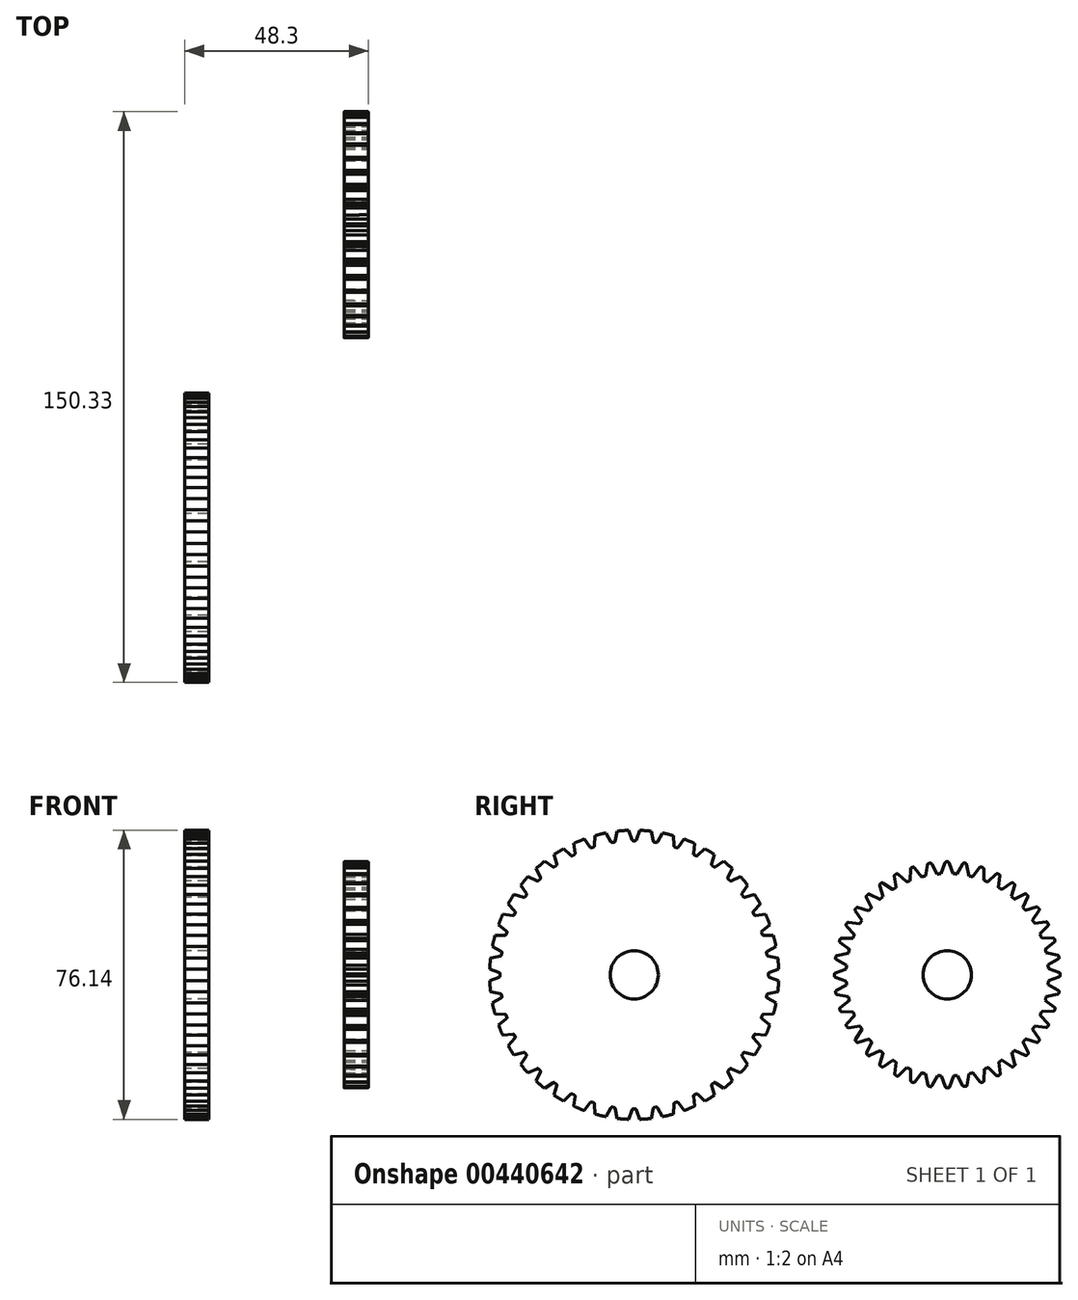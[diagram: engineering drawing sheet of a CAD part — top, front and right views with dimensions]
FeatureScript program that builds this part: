
annotation { "Feature Type Name" : "Feature", "Feature Type Description" : "" }
export const myFeature = defineFeature(function(context is Context, id is Id, definition is map)
    precondition{}
    {
        {
            var Q0;
            Q0=qCreatedBy(makeId("Front.planeOp"),FACE);
            var sketch = newSketch(context, id + "F0", { "sketchPlane" : qUnion([Q0])});
            skLineSegment(sketch, "E0", {"start": v(-6.35, 0) * mm, "end": v(0, 0) * mm, "construction": true});
            skLineSegment(sketch, "E1", {"start": v(0, 38.1) * mm, "end": v(0, -0.58) * mm, "construction": true});
            skLineSegment(sketch, "E2.bottom", {"start": v(0, 38.1) * mm, "end": v(-6.35, 38.1) * mm});
            skLineSegment(sketch, "E2.top", {"start": v(0, 6.35) * mm, "end": v(-6.35, 6.35) * mm});
            skLineSegment(sketch, "E2.left", {"start": v(0, 38.1) * mm, "end": v(0, 6.35) * mm});
            skLineSegment(sketch, "E2.right", {"start": v(-6.35, 38.1) * mm, "end": v(-6.35, 6.35) * mm});
            skSolve(sketch);
        }
        {
            var Q0;
            Q0=makeQuery(id+"F0.imprint","IMPRINT",FACE,{"disambiguationData":[TD([[makeQuery(id+"F0.imprint","IMPRINT",EDGE,{"derivedFrom":sQuery(id+"F0.wireOp",EDGE,"E2.bottom")}),1.0]])]});
            var Q1;
            Q1=sQuery(id+"F0.wireOp",EDGE,"E0");
            revolve(context, id + "F1", {"entities" : qUnion([Q0]), "axis" : qUnion([Q1]), "revolveType" : RevolveType.FULL});
        }
        {
            var Q0;
            Q0=qCreatedBy(makeId("Right.planeOp"),FACE);
            var sketch = newSketch(context, id + "F2", { "sketchPlane" : qUnion([Q0])});
            skLineSegment(sketch, "E3", {"start": v(0, 0) * mm, "end": v(0, 38.15) * mm, "construction": true});
            skArc(sketch, "E4", {"start": v(0.51, 35.34) * mm, "mid": v(0, 35.35) * mm, "end": v(-0.51, 35.34) * mm});
            skLineSegment(sketch, "E5", {"start": v(1.53, 38.13) * mm, "end": v(0.6, 35.6) * mm});
            skLineSegment(sketch, "E6.MirrorCS", {"start": v(-1.53, 38.13) * mm, "end": v(-0.6, 35.6) * mm});
            skLineSegment(sketch, "E7", {"start": v(-0.24, 35.34) * mm, "end": v(0.24, 35.34) * mm});
            skPoint(sketch, "E8.visualSharp", {"position": v(-0.51, 35.34) * mm});
            skArc(sketch, "E8.filletArc", {"start": v(-0.6, 35.6) * mm, "mid": v(-0.46, 35.41) * mm, "end": v(-0.24, 35.34) * mm});
            skPoint(sketch, "E9.visualSharp", {"position": v(0.51, 35.34) * mm});
            skArc(sketch, "E9.filletArc", {"start": v(0.24, 35.34) * mm, "mid": v(0.46, 35.41) * mm, "end": v(0.6, 35.6) * mm});
            skLineSegment(sketch, "E10", {"start": v(-1.53, 38.13) * mm, "end": v(0, 38.15) * mm});
            skLineSegment(sketch, "E11", {"start": v(0, 38.15) * mm, "end": v(1.53, 38.13) * mm});
            skSolve(sketch);
        }
        {
            var Q0;
            Q0 = qSketchRegion(id + "F2", true);
            extrude(context, id + "F3", {"entities" : qUnion([Q0]), "operationType" : NewBodyOperationType.REMOVE, "endBound" : BoundingType.SYMMETRIC, "depth" : 12.7 * mm});
        }
        {
            var Q0;
            Q0=makeQuery(id+"F3.boolean.opBoolean","COPY",FACE,{"derivedFrom":makeQuery(id+"F3.opExtrude","SWEPT_FACE",FACE,{"disambiguationData":[OSD([sQuery(id+"F2.wireOp",EDGE,"E6.MirrorCS")])]})});
            var Q1;
            Q1=makeQuery(id+"F3.boolean.opBoolean","COPY",FACE,{"derivedFrom":makeQuery(id+"F3.opExtrude","SWEPT_FACE",FACE,{"disambiguationData":[OSD([sQuery(id+"F2.wireOp",EDGE,"E8.filletArc")])]})});
            var Q2;
            Q2=makeQuery(id+"F3.boolean.opBoolean","COPY",FACE,{"derivedFrom":makeQuery(id+"F3.opExtrude","SWEPT_FACE",FACE,{"disambiguationData":[OSD([sQuery(id+"F2.wireOp",EDGE,"E7")])]})});
            var Q3;
            Q3=makeQuery(id+"F3.boolean.opBoolean","COPY",FACE,{"derivedFrom":makeQuery(id+"F3.opExtrude","SWEPT_FACE",FACE,{"disambiguationData":[OSD([sQuery(id+"F2.wireOp",EDGE,"E9.filletArc")])]})});
            var Q4;
            Q4=makeQuery(id+"F3.boolean.opBoolean","COPY",FACE,{"derivedFrom":makeQuery(id+"F3.opExtrude","SWEPT_FACE",FACE,{"disambiguationData":[OSD([sQuery(id+"F2.wireOp",EDGE,"E5")])]})});
            var Q5;
            Q5=makeQuery(id+"F1.opRevolve","SWEPT_EDGE",EDGE,{"disambiguationData":[OSD([sQuery(id+"F0.wireOp",EDGE,"E2.top"),sQuery(id+"F0.wireOp",EDGE,"E2.left")])]});
            circularPattern(context, id + "F4", {"patternType" : PatternType.FACE, "operationType" : NewBodyOperationType.REMOVE, "faces" : qUnion([Q0, Q1, Q2, Q3, Q4]), "axis" : qUnion([Q5]), "angle" : 9 * degree, "instanceCount" : 40});
        }
        {
            var Q0;
            Q0=qCreatedBy(makeId("Top.planeOp"),FACE);
            var sketch = newSketch(context, id + "F5", { "sketchPlane" : qUnion([Q0])});
            skLineSegment(sketch, "E12", {"start": v(35.6, 109.16) * mm, "end": v(35.6, 88.84) * mm});
            skLineSegment(sketch, "E13", {"start": v(38.77, 88.84) * mm, "end": v(38.77, 109.17) * mm});
            skLineSegment(sketch, "E14.MirrorCS", {"start": v(41.95, 109.18) * mm, "end": v(41.95, 88.84) * mm});
            skLineSegment(sketch, "E15", {"start": v(38.77, 82.5) * mm, "end": v(38.77, 114.37) * mm, "construction": true});
            skLineSegment(sketch, "E16", {"start": v(38.77, 82.5) * mm, "end": v(28.33, 82.5) * mm, "construction": true});
            skLineSegment(sketch, "E17", {"start": v(35.6, 109.16) * mm, "end": v(41.95, 109.18) * mm});
            skLineSegment(sketch, "E18", {"start": v(35.6, 88.84) * mm, "end": v(41.95, 88.84) * mm});
            skSolve(sketch);
        }
        {
            var Q0;
            {var subQ0=sQuery(id+"F5.wireOp",EDGE,"E12");Q0=makeQuery(id+"F5.imprint","IMPRINT",FACE,{"disambiguationData":[TD([[makeQuery(id+"F5.imprint","IMPRINT",EDGE,{"derivedFrom":subQ0}),1.0]])]});}
            var Q1;
            {var subQ0=sQuery(id+"F5.wireOp",EDGE,"E13");Q1=makeQuery(id+"F5.imprint","IMPRINT",FACE,{"disambiguationData":[TD([[makeQuery(id+"F5.imprint","IMPRINT",EDGE,{"derivedFrom":subQ0}),-1.0]])]});}
            var Q2;
            Q2=sQuery(id+"F5.wireOp",EDGE,"E16");
            revolve(context, id + "F6", {"entities" : qUnion([Q0, Q1]), "axis" : qUnion([Q2]), "revolveType" : RevolveType.FULL});
        }
        {
            var Q0;
            Q0=makeQuery(id+"F6.opRevolve","SWEPT_FACE",FACE,{"disambiguationData":[OSD([sQuery(id+"F5.wireOp",EDGE,"E14.MirrorCS")])]});
            var sketch = newSketch(context, id + "F7", { "sketchPlane" : qUnion([Q0])});
            skArc(sketch, "E19", {"start": v(5.08, 22.05) * mm, "mid": v(4.56, 22.05) * mm, "end": v(4.05, 22.05) * mm});
            skLineSegment(sketch, "E20", {"start": v(6.09, 24.83) * mm, "end": v(5.17, 22.3) * mm});
            skArc(sketch, "E21.filletArc", {"start": v(4.8, 22.05) * mm, "mid": v(5.03, 22.12) * mm, "end": v(5.17, 22.3) * mm});
            skLineSegment(sketch, "E22", {"start": v(4.56, 24.85) * mm, "end": v(6.09, 24.83) * mm});
            skLineSegment(sketch, "E23", {"start": v(4.56, 24.85) * mm, "end": v(4.6, 22.05) * mm});
            skArc(sketch, "E24", {"start": v(8.2, 22.26) * mm, "mid": v(7.7, 22.26) * mm, "end": v(7.18, 22.26) * mm});
            skLineSegment(sketch, "E25", {"start": v(9.22, 25.04) * mm, "end": v(8.3, 22.52) * mm});
            skLineSegment(sketch, "E26.MirrorCS", {"start": v(6.16, 25.04) * mm, "end": v(7.08, 22.52) * mm});
            skLineSegment(sketch, "E27", {"start": v(7.45, 22.26) * mm, "end": v(7.93, 22.26) * mm});
            skPoint(sketch, "E28.visualSharp", {"position": v(7.18, 22.26) * mm});
            skArc(sketch, "E28.filletArc", {"start": v(7.08, 22.52) * mm, "mid": v(7.23, 22.33) * mm, "end": v(7.45, 22.26) * mm});
            skPoint(sketch, "E29.visualSharp", {"position": v(8.2, 22.26) * mm});
            skArc(sketch, "E29.filletArc", {"start": v(7.93, 22.26) * mm, "mid": v(8.16, 22.33) * mm, "end": v(8.3, 22.52) * mm});
            skLineSegment(sketch, "E30", {"start": v(6.16, 25.04) * mm, "end": v(7.7, 25.06) * mm});
            skLineSegment(sketch, "E31", {"start": v(7.7, 25.06) * mm, "end": v(9.22, 25.04) * mm});
            skLineSegment(sketch, "E32", {"start": v(7.7, 25.06) * mm, "end": v(7.72, 22.26) * mm});
            skCircle(sketch, "E33", {"center": v(82.5, 0) * mm, "radius": 25.38 * mm});
            skLineSegment(sketch, "E34", {"start": v(82.5, 0) * mm, "end": v(82.5, 39.5) * mm, "construction": true});
            skArc(sketch, "E35", {"start": v(81.99, 29.77) * mm, "mid": v(82.45, 29.76) * mm, "end": v(82.9, 29.76) * mm});
            skLineSegment(sketch, "E36", {"start": v(80.83, 26.51) * mm, "end": v(81.9, 29.5) * mm});
            skLineSegment(sketch, "E37.MirrorCS", {"start": v(84.07, 26.51) * mm, "end": v(83, 29.5) * mm});
            skLineSegment(sketch, "E38", {"start": v(82.63, 29.77) * mm, "end": v(82.26, 29.77) * mm});
            skPoint(sketch, "E39.visualSharp", {"position": v(82.9, 29.76) * mm});
            skArc(sketch, "E39.filletArc", {"start": v(83, 29.5) * mm, "mid": v(82.86, 29.7) * mm, "end": v(82.63, 29.77) * mm});
            skPoint(sketch, "E40.visualSharp", {"position": v(81.99, 29.77) * mm});
            skArc(sketch, "E40.filletArc", {"start": v(82.26, 29.77) * mm, "mid": v(82.04, 29.7) * mm, "end": v(81.9, 29.5) * mm});
            skLineSegment(sketch, "E41", {"start": v(84.07, 26.51) * mm, "end": v(82.5, 26.51) * mm});
            skLineSegment(sketch, "E42", {"start": v(82.5, 26.51) * mm, "end": v(80.83, 26.51) * mm});
            skLineSegment(sketch, "E43", {"start": v(82.5, 26.51) * mm, "end": v(82.5, 29.76) * mm});
            skSolve(sketch);
        }
        {
            var Q0;
            {var subQ0=sQuery(id+"F7.wireOp",EDGE,"E43");var subQ1=sQuery(id+"F7.wireOp",EDGE,"E35");var subQ2=makeQuery(id+"F7.imprint","INTERSECT",VERTEX,{"derivedFrom":[subQ1,subQ0]});Q0=makeQuery(id+"F7.imprint","IMPRINT",FACE,{"disambiguationData":[TD([[makeQuery(id+"F7.imprint","IMPRINT",EDGE,{"disambiguationData":[TD([[subQ2,1.0]])],"derivedFrom":subQ1}),-1.0]])]});}
            var Q1;
            {var subQ0=sQuery(id+"F7.wireOp",EDGE,"E43");var subQ1=sQuery(id+"F7.wireOp",EDGE,"E35");var subQ2=makeQuery(id+"F7.imprint","INTERSECT",VERTEX,{"derivedFrom":[subQ1,subQ0]});Q1=makeQuery(id+"F7.imprint","IMPRINT",FACE,{"disambiguationData":[TD([[makeQuery(id+"F7.imprint","IMPRINT",EDGE,{"disambiguationData":[TD([[subQ2,-1.0]])],"derivedFrom":subQ1}),-1.0]])]});}
            var Q2;
            {var subQ0=sQuery(id+"F7.wireOp",EDGE,"E42");Q2=makeQuery(id+"F7.imprint","IMPRINT",FACE,{"disambiguationData":[TD([[makeQuery(id+"F7.imprint","IMPRINT",EDGE,{"derivedFrom":subQ0}),-1.0]])]});}
            var Q3;
            {var subQ0=sQuery(id+"F7.wireOp",EDGE,"E41");Q3=makeQuery(id+"F7.imprint","IMPRINT",FACE,{"disambiguationData":[TD([[makeQuery(id+"F7.imprint","IMPRINT",EDGE,{"derivedFrom":subQ0}),-1.0]])]});}
            extrude(context, id + "F8", {"entities" : qUnion([Q0, Q1, Q2, Q3]), "operationType" : NewBodyOperationType.ADD, "oppositeDirection" : true, "depth" : 6.35 * mm});
        }
        {
            var Q0;
            Q0=makeQuery(id+"F8.opExtrude","SWEPT_FACE",FACE,{"disambiguationData":[OSD([sQuery(id+"F7.wireOp",EDGE,"E37.MirrorCS")])]});
            var Q1;
            Q1=makeQuery(id+"F8.opExtrude","SWEPT_FACE",FACE,{"disambiguationData":[OSD([sQuery(id+"F7.wireOp",EDGE,"E39.filletArc")])]});
            var Q2;
            Q2=makeQuery(id+"F8.opExtrude","SWEPT_FACE",FACE,{"disambiguationData":[OSD([sQuery(id+"F7.wireOp",EDGE,"E35")])]});
            var Q3;
            Q3=makeQuery(id+"F8.opExtrude","SWEPT_FACE",FACE,{"disambiguationData":[OSD([sQuery(id+"F7.wireOp",EDGE,"E40.filletArc")])]});
            var Q4;
            Q4=makeQuery(id+"F8.opExtrude","SWEPT_FACE",FACE,{"disambiguationData":[OSD([sQuery(id+"F7.wireOp",EDGE,"E36")])]});
            var Q5;
            Q5=makeQuery(id+"F6.opRevolve","SWEPT_EDGE",EDGE,{"disambiguationData":[OSD([sQuery(id+"F5.wireOp",EDGE,"E14.MirrorCS"),sQuery(id+"F5.wireOp",EDGE,"E18")])]});
            circularPattern(context, id + "F9", {"patternType" : PatternType.FACE, "faces" : qUnion([Q0, Q1, Q2, Q3, Q4]), "axis" : qUnion([Q5]), "angle" : 360 * degree, "instanceCount" : 40, "equalSpace" : true});
        }
    });
